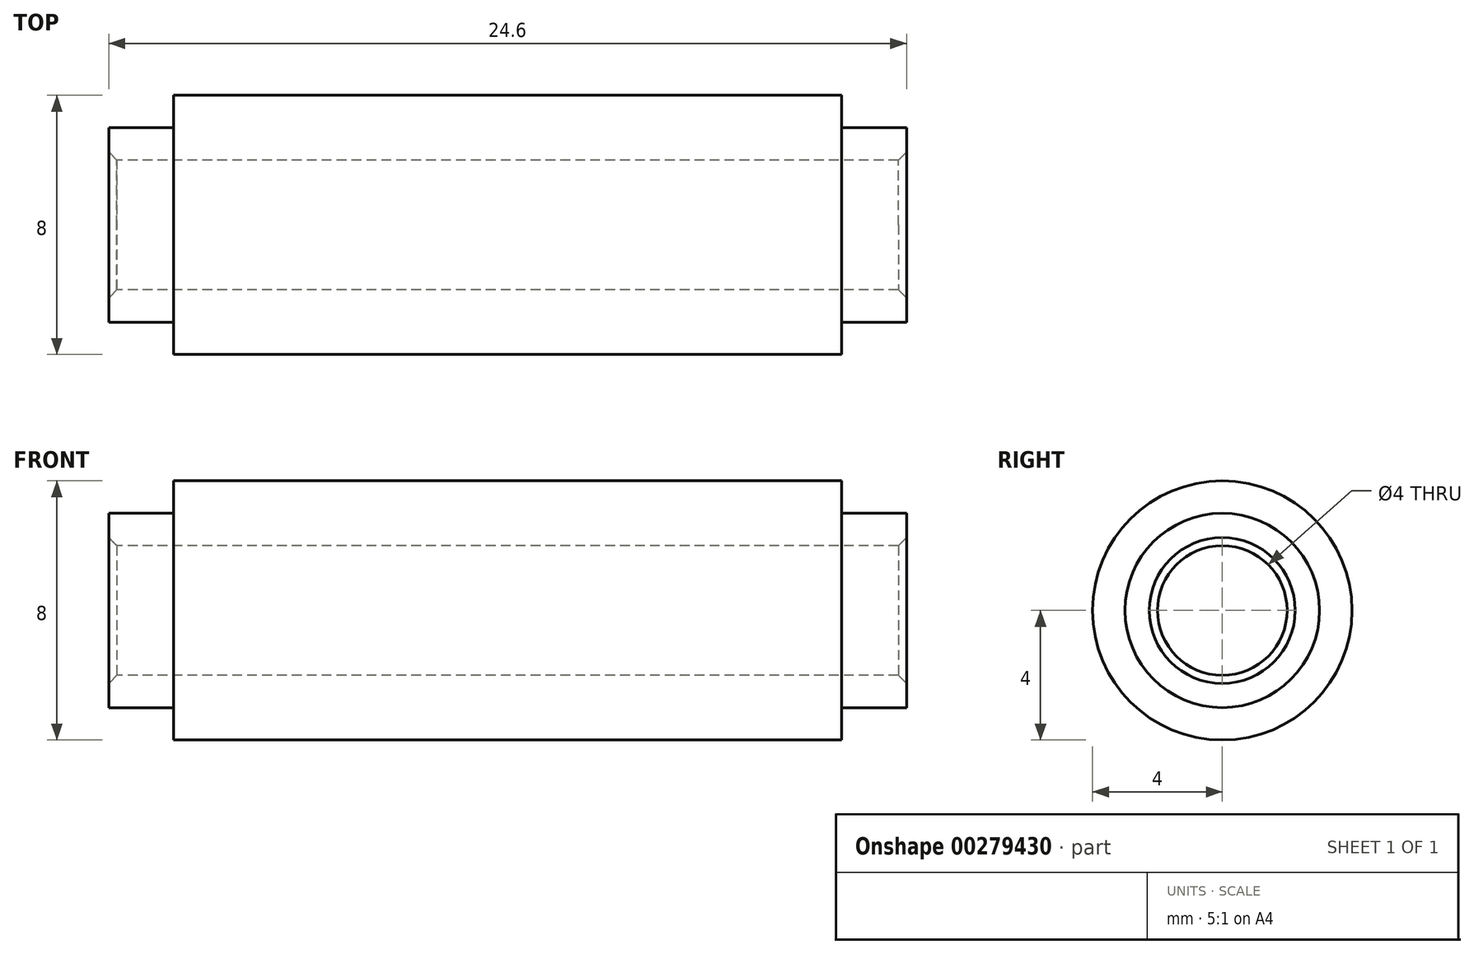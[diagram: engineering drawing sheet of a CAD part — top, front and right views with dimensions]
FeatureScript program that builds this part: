
annotation { "Feature Type Name" : "Feature", "Feature Type Description" : "" }
export const myFeature = defineFeature(function(context is Context, id is Id, definition is map)
    precondition{}
    {
        {
            var Q0;
            Q0=qCreatedBy(makeId("Front.planeOp"),FACE);
            var sketch = newSketch(context, id + "F0", { "sketchPlane" : qUnion([Q0])});
            skLineSegment(sketch, "E0", {"start": v(-104.5, 0) * mm, "end": v(-1.77, 0) * mm, "construction": true});
            skLineSegment(sketch, "E1", {"start": v(0, 51.36) * mm, "end": v(0, -51.36) * mm, "construction": true});
            skLineSegment(sketch, "E2", {"start": v(-12.3, -2) * mm, "end": v(-12.3, -3) * mm});
            skLineSegment(sketch, "E3", {"start": v(-12.3, -3) * mm, "end": v(-10.3, -3) * mm});
            skLineSegment(sketch, "E4", {"start": v(-10.3, -3) * mm, "end": v(-10.3, -4) * mm});
            skLineSegment(sketch, "E5", {"start": v(-10.3, -4) * mm, "end": v(10.3, -4) * mm});
            skLineSegment(sketch, "E6", {"start": v(10.3, -4) * mm, "end": v(10.3, -3) * mm});
            skLineSegment(sketch, "E7", {"start": v(10.3, -3) * mm, "end": v(12.3, -3) * mm});
            skLineSegment(sketch, "E8", {"start": v(12.3, -3) * mm, "end": v(12.3, -2) * mm});
            skLineSegment(sketch, "E9", {"start": v(12.3, -2) * mm, "end": v(-12.3, -2) * mm});
            skSolve(sketch);
        }
        {
            var Q0;
            Q0=makeQuery(id+"F0.imprint","IMPRINT",FACE,{"disambiguationData":[TD([[makeQuery(id+"F0.imprint","IMPRINT",EDGE,{"derivedFrom":sQuery(id+"F0.wireOp",EDGE,"E2")}),1.0]])]});
            var Q1;
            Q1=sQuery(id+"F0.wireOp",EDGE,"E0");
            revolve(context, id + "F1", {"entities" : qUnion([Q0]), "axis" : qUnion([Q1]), "revolveType" : RevolveType.FULL});
        }
        {
            var Q0;
            Q0=makeQuery(id+"F1.opRevolve","SWEPT_FACE",FACE,{"disambiguationData":[OSD([sQuery(id+"F0.wireOp",EDGE,"E9")])]});
            chamfer(context, id + "F2", {"entities" : qUnion([Q0]), "chamferType" : ChamferType.OFFSET_ANGLE, "width" : .25 * mm, "oppositeDirection" : false, "angle" : 45 * degree, "tangentPropagation" : true});
        }
    });
